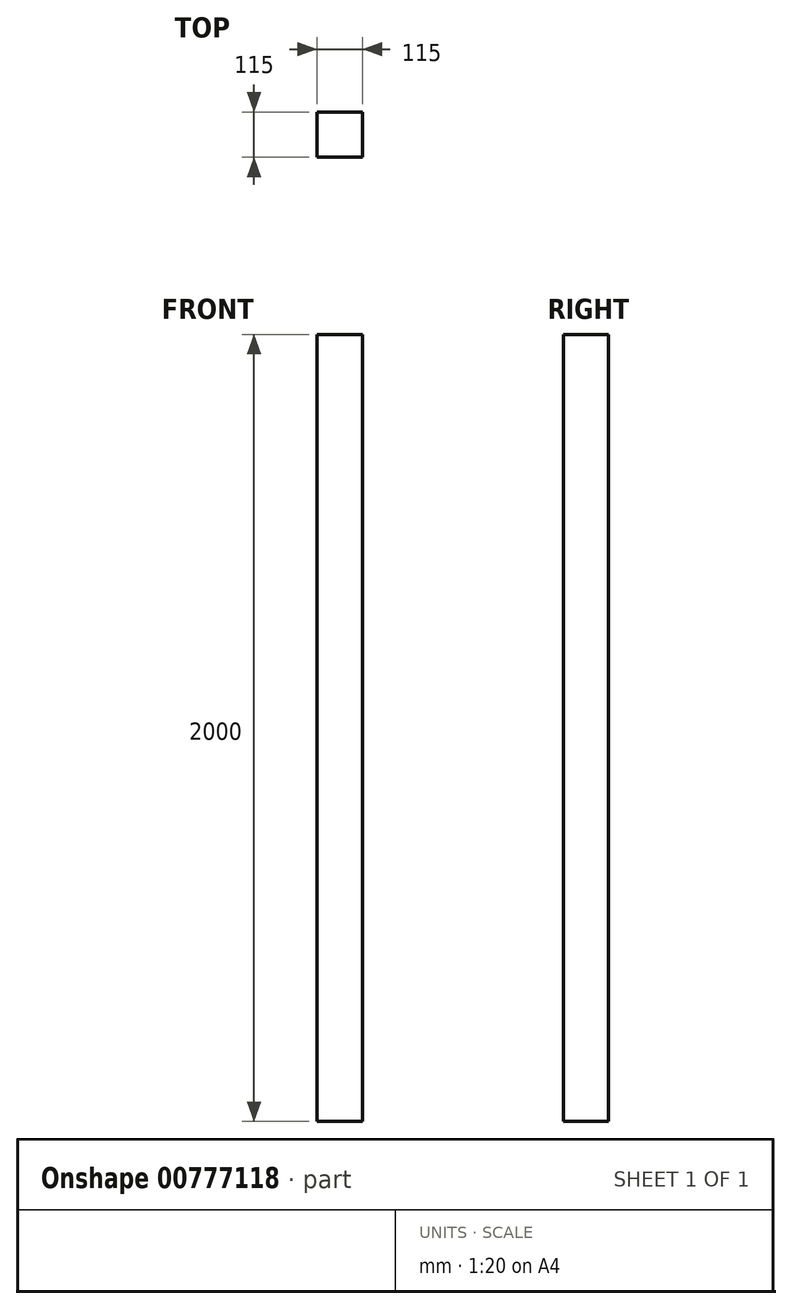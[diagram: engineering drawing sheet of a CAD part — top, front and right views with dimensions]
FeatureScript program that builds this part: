
annotation { "Feature Type Name" : "Feature", "Feature Type Description" : "" }
export const myFeature = defineFeature(function(context is Context, id is Id, definition is map)
    precondition{}
    {
        {
            var Q0;
            Q0=qCreatedBy(makeId("Top.planeOp"),FACE);
            var sketch = newSketch(context, id + "F0", { "sketchPlane" : qUnion([Q0])});
            skLineSegment(sketch, "E0.bottom", {"start": v(-57.5, 57.5) * mm, "end": v(57.5, 57.5) * mm});
            skLineSegment(sketch, "E0.top", {"start": v(-57.5, -57.5) * mm, "end": v(57.5, -57.5) * mm});
            skLineSegment(sketch, "E0.left", {"start": v(-57.5, 57.5) * mm, "end": v(-57.5, -57.5) * mm});
            skLineSegment(sketch, "E0.right", {"start": v(57.5, 57.5) * mm, "end": v(57.5, -57.5) * mm});
            skPoint(sketch, "E0.middle", {"position": v(0, 0) * mm});
            skSolve(sketch);
        }
        {
            var Q0;
            Q0=makeQuery(id+"F0.imprint","IMPRINT",FACE,{"disambiguationData":[TD([[makeQuery(id+"F0.imprint","IMPRINT",EDGE,{"derivedFrom":sQuery(id+"F0.wireOp",EDGE,"E0.bottom")}),-1.0]])]});
            extrude(context, id + "F1", {"entities" : qUnion([Q0]), "depth" : 2000 * mm, "offsetDistance" : 25 * mm});
        }
    });
